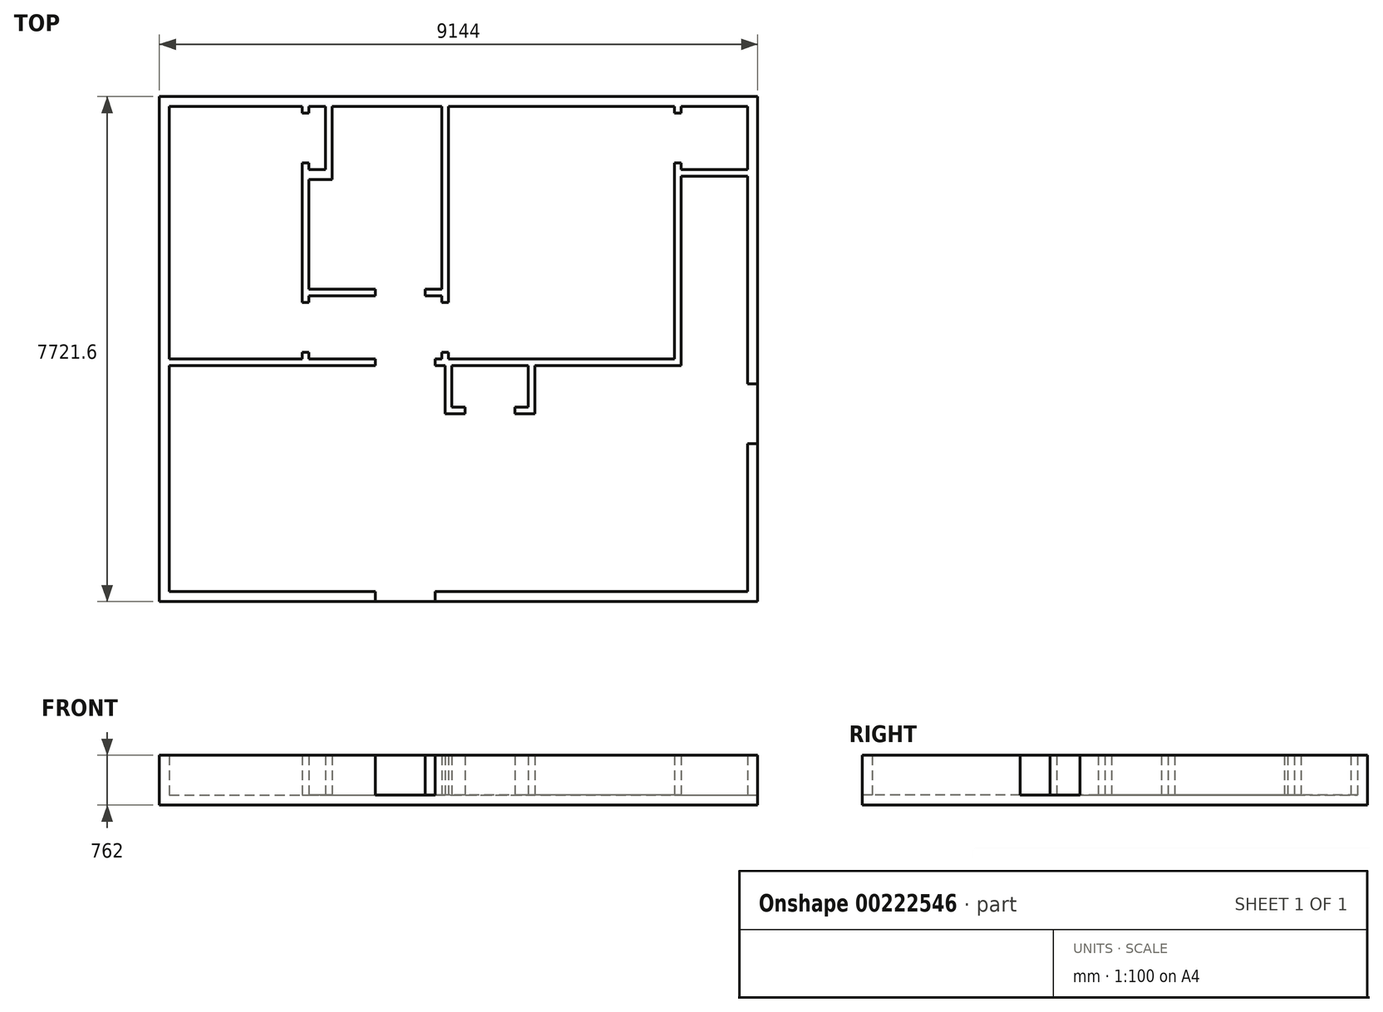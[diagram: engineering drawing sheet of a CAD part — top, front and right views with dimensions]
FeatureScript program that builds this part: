
annotation { "Feature Type Name" : "Feature", "Feature Type Description" : "" }
export const myFeature = defineFeature(function(context is Context, id is Id, definition is map)
    precondition{}
    {
        {
            var Q0;
            Q0=qCreatedBy(makeId("Top.planeOp"),FACE);
            var sketch = newSketch(context, id + "F0", { "sketchPlane" : qUnion([Q0])});
            skLineSegment(sketch, "E0", {"start": v(1574.8, 1727.2) * mm, "end": v(-1574.8, 1727.2) * mm});
            skLineSegment(sketch, "E1", {"start": v(-1574.8, 1727.2) * mm, "end": v(-1574.8, -1727.2) * mm});
            skLineSegment(sketch, "E2", {"start": v(-1574.8, -1727.2) * mm, "end": v(1574.8, -1727.2) * mm});
            skLineSegment(sketch, "E3", {"start": v(1574.8, -1727.2) * mm, "end": v(1574.8, -1879.6) * mm});
            skLineSegment(sketch, "E4", {"start": v(1574.8, -1879.6) * mm, "end": v(-1727.2, -1879.6) * mm});
            skLineSegment(sketch, "E5", {"start": v(-1727.2, -1879.6) * mm, "end": v(-1727.2, 1828.8) * mm});
            skLineSegment(sketch, "E6", {"start": v(-1727.2, 1828.8) * mm, "end": v(457.2, 1828.8) * mm});
            skLineSegment(sketch, "E7", {"start": v(1574.8, 1828.8) * mm, "end": v(1574.8, 1727.2) * mm});
            skLineSegment(sketch, "E8", {"start": v(2489.2, -1727.2) * mm, "end": v(2489.2, -1879.6) * mm});
            skLineSegment(sketch, "E9", {"start": v(2489.2, -1879.6) * mm, "end": v(7416.8, -1879.6) * mm});
            skLineSegment(sketch, "E10", {"start": v(6248.4, 3430.75) * mm, "end": v(6248.4, 1727.2) * mm});
            skLineSegment(sketch, "E11", {"start": v(6248.4, 1727.2) * mm, "end": v(4013.2, 1727.2) * mm});
            skLineSegment(sketch, "E12", {"start": v(4013.2, 1727.2) * mm, "end": v(4013.2, 990.6) * mm});
            skLineSegment(sketch, "E13", {"start": v(4013.2, 990.6) * mm, "end": v(3708.4, 990.6) * mm});
            skLineSegment(sketch, "E14", {"start": v(2641.6, 990.6) * mm, "end": v(2641.6, 1727.2) * mm});
            skLineSegment(sketch, "E15", {"start": v(2641.6, 1727.2) * mm, "end": v(2489.2, 1727.2) * mm});
            skLineSegment(sketch, "E16", {"start": v(2489.2, 1727.2) * mm, "end": v(2489.2, 1828.8) * mm});
            skLineSegment(sketch, "E17", {"start": v(2489.2, 1828.8) * mm, "end": v(2590.8, 1828.8) * mm});
            skLineSegment(sketch, "E18", {"start": v(2590.8, 1828.8) * mm, "end": v(2590.8, 1930.4) * mm});
            skLineSegment(sketch, "E19", {"start": v(2590.8, 1930.4) * mm, "end": v(2692.4, 1930.4) * mm});
            skLineSegment(sketch, "E20", {"start": v(2692.4, 1930.4) * mm, "end": v(2692.4, 1828.8) * mm});
            skLineSegment(sketch, "E21", {"start": v(2692.4, 1828.8) * mm, "end": v(6146.8, 1828.8) * mm});
            skLineSegment(sketch, "E22", {"start": v(6146.8, 1828.8) * mm, "end": v(6146.8, 4826) * mm});
            skLineSegment(sketch, "E23", {"start": v(2489.2, -1727.2) * mm, "end": v(7264.4, -1727.2) * mm});
            skLineSegment(sketch, "E24", {"start": v(7264.4, -1727.2) * mm, "end": v(7264.4, 533.4) * mm});
            skLineSegment(sketch, "E25", {"start": v(6146.8, 5689.6) * mm, "end": v(2692.4, 5689.6) * mm});
            skLineSegment(sketch, "E26", {"start": v(2692.4, 5689.6) * mm, "end": v(2692.4, 2692.4) * mm});
            skLineSegment(sketch, "E27", {"start": v(2692.4, 2692.4) * mm, "end": v(2590.8, 2692.4) * mm});
            skLineSegment(sketch, "E28", {"start": v(2590.8, 2692.4) * mm, "end": v(2590.8, 2794) * mm});
            skLineSegment(sketch, "E29", {"start": v(2590.8, 2794) * mm, "end": v(2336.8, 2794) * mm});
            skLineSegment(sketch, "E30", {"start": v(2336.8, 2794) * mm, "end": v(2336.8, 2895.6) * mm});
            skLineSegment(sketch, "E31", {"start": v(2336.8, 2895.6) * mm, "end": v(2590.8, 2895.6) * mm});
            skLineSegment(sketch, "E32", {"start": v(2590.8, 2895.6) * mm, "end": v(2590.8, 5689.6) * mm});
            skLineSegment(sketch, "E33", {"start": v(2590.8, 5842) * mm, "end": v(1396.88, 5842) * mm});
            skLineSegment(sketch, "E34", {"start": v(558.8, 2895.6) * mm, "end": v(1574.8, 2895.6) * mm});
            skLineSegment(sketch, "E35", {"start": v(1574.8, 2895.6) * mm, "end": v(1574.8, 2794) * mm});
            skLineSegment(sketch, "E36", {"start": v(1574.8, 2794) * mm, "end": v(558.8, 2794) * mm});
            skLineSegment(sketch, "E37", {"start": v(558.8, 2794) * mm, "end": v(558.8, 2692.4) * mm});
            skLineSegment(sketch, "E38", {"start": v(558.8, 2692.4) * mm, "end": v(457.2, 2692.4) * mm});
            skLineSegment(sketch, "E39", {"start": v(457.2, 2692.4) * mm, "end": v(457.2, 4724.4) * mm});
            skLineSegment(sketch, "E40", {"start": v(812.8, 4724.4) * mm, "end": v(812.8, 5689.6) * mm});
            skLineSegment(sketch, "E41", {"start": v(812.8, 5689.6) * mm, "end": v(558.8, 5689.6) * mm});
            skLineSegment(sketch, "E42", {"start": v(-1574.8, 5689.6) * mm, "end": v(-1574.8, 1828.8) * mm});
            skLineSegment(sketch, "E43", {"start": v(-1727.2, 1828.8) * mm, "end": v(-1727.2, 5842) * mm});
            skLineSegment(sketch, "E44", {"start": v(-1727.2, 5842) * mm, "end": v(1396.88, 5842) * mm});
            skLineSegment(sketch, "E45", {"start": v(914.4, 4572) * mm, "end": v(558.8, 4572) * mm});
            skLineSegment(sketch, "E46", {"start": v(558.8, 4572) * mm, "end": v(558.8, 2895.6) * mm});
            skLineSegment(sketch, "E47", {"start": v(457.2, 4724.4) * mm, "end": v(457.2, 4826) * mm});
            skLineSegment(sketch, "E48", {"start": v(457.2, 4826) * mm, "end": v(558.8, 4826) * mm});
            skLineSegment(sketch, "E49", {"start": v(558.8, 4826) * mm, "end": v(558.8, 4724.4) * mm});
            skLineSegment(sketch, "E50", {"start": v(457.2, 5689.6) * mm, "end": v(457.2, 5588) * mm});
            skLineSegment(sketch, "E51", {"start": v(457.2, 5588) * mm, "end": v(558.8, 5588) * mm});
            skLineSegment(sketch, "E52", {"start": v(558.8, 5588) * mm, "end": v(558.8, 5689.6) * mm});
            skLineSegment(sketch, "E53.trimOffspring", {"start": v(457.2, 5689.6) * mm, "end": v(-1574.8, 5689.6) * mm});
            skLineSegment(sketch, "E54", {"start": v(558.8, 4724.4) * mm, "end": v(812.8, 4724.4) * mm});
            skLineSegment(sketch, "E55", {"start": v(457.2, 1828.8) * mm, "end": v(457.2, 1930.4) * mm});
            skLineSegment(sketch, "E56", {"start": v(457.2, 1930.4) * mm, "end": v(558.8, 1930.4) * mm});
            skLineSegment(sketch, "E57", {"start": v(558.8, 1930.4) * mm, "end": v(558.8, 1828.8) * mm});
            skLineSegment(sketch, "E58.trimOffspring", {"start": v(558.8, 1828.8) * mm, "end": v(1574.8, 1828.8) * mm});
            skLineSegment(sketch, "E59", {"start": v(2590.8, 5842) * mm, "end": v(7416.8, 5842) * mm});
            skLineSegment(sketch, "E60", {"start": v(6248.4, 3430.75) * mm, "end": v(6248.4, 4622.8) * mm});
            skLineSegment(sketch, "E61", {"start": v(2946.4, 990.6) * mm, "end": v(2946.4, 1092.2) * mm});
            skLineSegment(sketch, "E62", {"start": v(2946.4, 1092.2) * mm, "end": v(2743.2, 1092.2) * mm});
            skLineSegment(sketch, "E63", {"start": v(2743.2, 1092.2) * mm, "end": v(2743.2, 1727.2) * mm});
            skLineSegment(sketch, "E64", {"start": v(2743.2, 1727.2) * mm, "end": v(3911.6, 1727.2) * mm});
            skLineSegment(sketch, "E65", {"start": v(3911.6, 1727.2) * mm, "end": v(3911.6, 1092.2) * mm});
            skLineSegment(sketch, "E66", {"start": v(3911.6, 1092.2) * mm, "end": v(3708.4, 1092.2) * mm});
            skLineSegment(sketch, "E67", {"start": v(3708.4, 1092.2) * mm, "end": v(3708.4, 990.6) * mm});
            skLineSegment(sketch, "E68.trimOffspring", {"start": v(2946.4, 990.6) * mm, "end": v(2641.6, 990.6) * mm});
            skLineSegment(sketch, "E69", {"start": v(914.4, 5689.6) * mm, "end": v(2590.8, 5689.6) * mm});
            skLineSegment(sketch, "E70", {"start": v(914.4, 5689.6) * mm, "end": v(914.4, 4572) * mm});
            skLineSegment(sketch, "E71", {"start": v(6248.4, 5689.6) * mm, "end": v(7264.4, 5689.6) * mm});
            skLineSegment(sketch, "E72", {"start": v(7416.8, 5842) * mm, "end": v(7416.8, 1447.8) * mm});
            skLineSegment(sketch, "E73", {"start": v(6248.4, 4724.4) * mm, "end": v(7264.4, 4724.4) * mm});
            skLineSegment(sketch, "E74", {"start": v(6146.8, 4826) * mm, "end": v(6248.4, 4826) * mm});
            skLineSegment(sketch, "E75", {"start": v(6146.8, 5588) * mm, "end": v(6248.4, 5588) * mm});
            skLineSegment(sketch, "E76.trimOffspring", {"start": v(6146.8, 5588) * mm, "end": v(6146.8, 5689.6) * mm});
            skLineSegment(sketch, "E77.trimOffspring", {"start": v(6248.4, 5588) * mm, "end": v(6248.4, 5689.6) * mm});
            skLineSegment(sketch, "E78", {"start": v(6248.4, 4622.8) * mm, "end": v(7264.4, 4622.8) * mm});
            skLineSegment(sketch, "E79.trimOffspring", {"start": v(6248.4, 4724.4) * mm, "end": v(6248.4, 4826) * mm});
            skLineSegment(sketch, "E80.trimOffspring", {"start": v(7264.4, 4724.4) * mm, "end": v(7264.4, 5689.6) * mm});
            skLineSegment(sketch, "E81", {"start": v(7264.4, 1447.8) * mm, "end": v(7416.8, 1447.8) * mm});
            skLineSegment(sketch, "E82", {"start": v(7264.4, 533.4) * mm, "end": v(7416.8, 533.4) * mm});
            skLineSegment(sketch, "E83.trimOffspring", {"start": v(7416.8, 533.4) * mm, "end": v(7416.8, -1879.6) * mm});
            skLineSegment(sketch, "E84.trimOffspring", {"start": v(7264.4, 1447.8) * mm, "end": v(7264.4, 4622.8) * mm});
            skSolve(sketch);
        }
        {
            var Q0;
            Q0 = qSketchRegion(id + "F0", true);
            extrude(context, id + "F1", {"entities" : qUnion([Q0]), "depth" : 609.6 * mm});
        }
        {
            var Q0;
            Q0=makeQuery(id+"F1.opExtrude","CAP_FACE",FACE,{"disambiguationData":[OSD([sQuery(id+"F0.wireOp",EDGE,"E0"),sQuery(id+"F0.wireOp",EDGE,"E1"),sQuery(id+"F0.wireOp",EDGE,"E2"),sQuery(id+"F0.wireOp",EDGE,"E3"),sQuery(id+"F0.wireOp",EDGE,"E4"),sQuery(id+"F0.wireOp",EDGE,"E5"),sQuery(id+"F0.wireOp",EDGE,"E6"),sQuery(id+"F0.wireOp",EDGE,"E7"),sQuery(id+"F0.wireOp",EDGE,"E8"),sQuery(id+"F0.wireOp",EDGE,"E9"),sQuery(id+"F0.wireOp",EDGE,"E10"),sQuery(id+"F0.wireOp",EDGE,"E11"),sQuery(id+"F0.wireOp",EDGE,"E12"),sQuery(id+"F0.wireOp",EDGE,"E13"),sQuery(id+"F0.wireOp",EDGE,"E14"),sQuery(id+"F0.wireOp",EDGE,"E15"),sQuery(id+"F0.wireOp",EDGE,"E16"),sQuery(id+"F0.wireOp",EDGE,"E17"),sQuery(id+"F0.wireOp",EDGE,"E18"),sQuery(id+"F0.wireOp",EDGE,"E19"),sQuery(id+"F0.wireOp",EDGE,"E20"),sQuery(id+"F0.wireOp",EDGE,"E21"),sQuery(id+"F0.wireOp",EDGE,"E22"),sQuery(id+"F0.wireOp",EDGE,"E23"),sQuery(id+"F0.wireOp",EDGE,"E24"),sQuery(id+"F0.wireOp",EDGE,"E25"),sQuery(id+"F0.wireOp",EDGE,"E26"),sQuery(id+"F0.wireOp",EDGE,"E27"),sQuery(id+"F0.wireOp",EDGE,"E28"),sQuery(id+"F0.wireOp",EDGE,"E29"),sQuery(id+"F0.wireOp",EDGE,"E30"),sQuery(id+"F0.wireOp",EDGE,"E31"),sQuery(id+"F0.wireOp",EDGE,"E32"),sQuery(id+"F0.wireOp",EDGE,"E33"),sQuery(id+"F0.wireOp",EDGE,"E34"),sQuery(id+"F0.wireOp",EDGE,"E35"),sQuery(id+"F0.wireOp",EDGE,"E36"),sQuery(id+"F0.wireOp",EDGE,"E37"),sQuery(id+"F0.wireOp",EDGE,"E38"),sQuery(id+"F0.wireOp",EDGE,"E39"),sQuery(id+"F0.wireOp",EDGE,"E40"),sQuery(id+"F0.wireOp",EDGE,"E41"),sQuery(id+"F0.wireOp",EDGE,"E42"),sQuery(id+"F0.wireOp",EDGE,"E43"),sQuery(id+"F0.wireOp",EDGE,"E44"),sQuery(id+"F0.wireOp",EDGE,"E45"),sQuery(id+"F0.wireOp",EDGE,"E46"),sQuery(id+"F0.wireOp",EDGE,"E47"),sQuery(id+"F0.wireOp",EDGE,"E48"),sQuery(id+"F0.wireOp",EDGE,"E49"),sQuery(id+"F0.wireOp",EDGE,"E50"),sQuery(id+"F0.wireOp",EDGE,"E51"),sQuery(id+"F0.wireOp",EDGE,"E52"),sQuery(id+"F0.wireOp",EDGE,"E53.trimOffspring"),sQuery(id+"F0.wireOp",EDGE,"E54"),sQuery(id+"F0.wireOp",EDGE,"E55"),sQuery(id+"F0.wireOp",EDGE,"E56"),sQuery(id+"F0.wireOp",EDGE,"E57"),sQuery(id+"F0.wireOp",EDGE,"E58.trimOffspring"),sQuery(id+"F0.wireOp",EDGE,"E59"),sQuery(id+"F0.wireOp",EDGE,"E60"),sQuery(id+"F0.wireOp",EDGE,"E61"),sQuery(id+"F0.wireOp",EDGE,"E62"),sQuery(id+"F0.wireOp",EDGE,"E63"),sQuery(id+"F0.wireOp",EDGE,"E64"),sQuery(id+"F0.wireOp",EDGE,"E65"),sQuery(id+"F0.wireOp",EDGE,"E66"),sQuery(id+"F0.wireOp",EDGE,"E67"),sQuery(id+"F0.wireOp",EDGE,"E68.trimOffspring"),sQuery(id+"F0.wireOp",EDGE,"E69"),sQuery(id+"F0.wireOp",EDGE,"E70"),sQuery(id+"F0.wireOp",EDGE,"E71"),sQuery(id+"F0.wireOp",EDGE,"E72"),sQuery(id+"F0.wireOp",EDGE,"E73"),sQuery(id+"F0.wireOp",EDGE,"E74"),sQuery(id+"F0.wireOp",EDGE,"E75"),sQuery(id+"F0.wireOp",EDGE,"E76.trimOffspring"),sQuery(id+"F0.wireOp",EDGE,"E77.trimOffspring"),sQuery(id+"F0.wireOp",EDGE,"E78"),sQuery(id+"F0.wireOp",EDGE,"E79.trimOffspring"),sQuery(id+"F0.wireOp",EDGE,"E80.trimOffspring")])],"isStart":true});
            var sketch = newSketch(context, id + "F2", { "sketchPlane" : qUnion([Q0])});
            skLineSegment(sketch, "E85.bottom", {"start": v(-1727.2, 1879.6) * mm, "end": v(7416.8, 1879.6) * mm});
            skLineSegment(sketch, "E85.top", {"start": v(-1727.2, -5842) * mm, "end": v(7416.8, -5842) * mm});
            skLineSegment(sketch, "E85.left", {"start": v(-1727.2, 1879.6) * mm, "end": v(-1727.2, -5842) * mm});
            skLineSegment(sketch, "E85.right", {"start": v(7416.8, 1879.6) * mm, "end": v(7416.8, -5842) * mm});
            skSolve(sketch);
        }
        {
            var Q0;
            Q0 = qSketchRegion(id + "F2", true);
            extrude(context, id + "F3", {"entities" : qUnion([Q0]), "operationType" : NewBodyOperationType.ADD, "depth" : 152.4 * mm});
        }
    });
